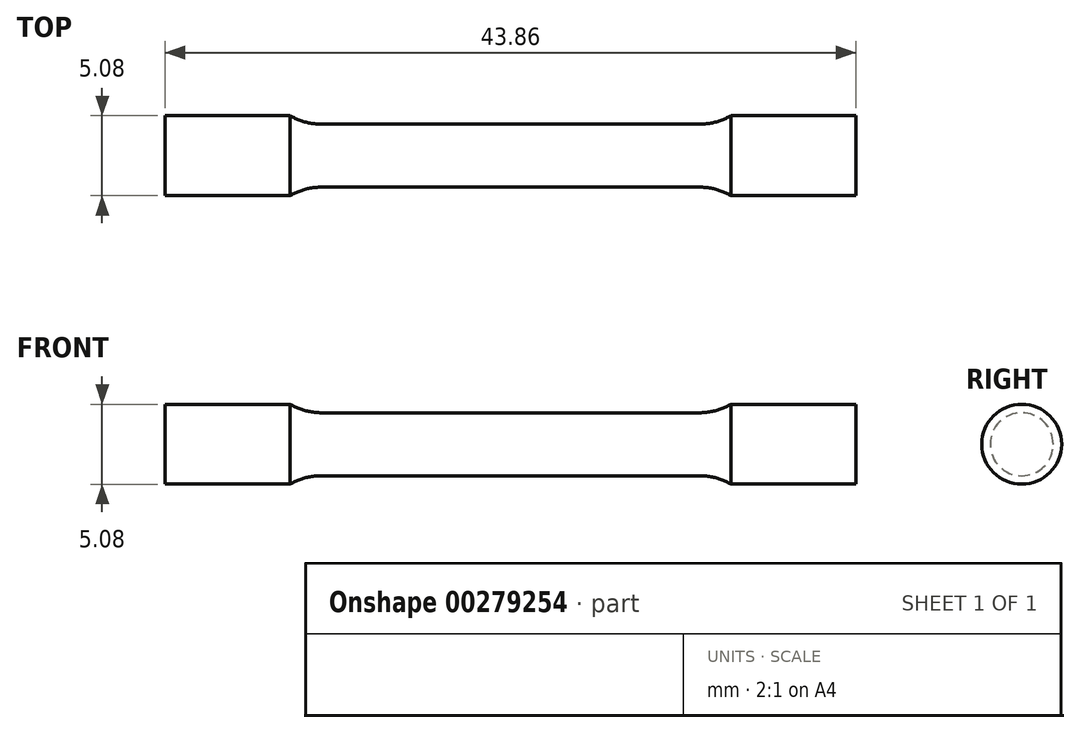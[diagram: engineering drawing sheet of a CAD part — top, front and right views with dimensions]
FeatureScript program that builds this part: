
annotation { "Feature Type Name" : "Feature", "Feature Type Description" : "" }
export const myFeature = defineFeature(function(context is Context, id is Id, definition is map)
    precondition{}
    {
        {
            var Q0;
            Q0=qCreatedBy(makeId("Front.planeOp"),FACE);
            var sketch = newSketch(context, id + "F0", { "sketchPlane" : qUnion([Q0])});
            skLineSegment(sketch, "E0", {"start": v(0, 2) * mm, "end": v(12, 2) * mm});
            skArc(sketch, "E1", {"start": v(12, 2) * mm, "mid": v(13.04, 2.14) * mm, "end": v(14, 2.54) * mm});
            skLineSegment(sketch, "E2", {"start": v(14, 2.54) * mm, "end": v(21.93, 2.54) * mm});
            skLineSegment(sketch, "E3", {"start": v(21.93, 2.54) * mm, "end": v(21.93, 0) * mm});
            skLineSegment(sketch, "E4.MirrorCS", {"start": v(-14, 2.54) * mm, "end": v(-21.93, 2.54) * mm});
            skLineSegment(sketch, "E5.MirrorCS", {"start": v(-21.93, 2.54) * mm, "end": v(-21.93, 0) * mm});
            skLineSegment(sketch, "E6.MirrorCS", {"start": v(0, 2) * mm, "end": v(-12, 2) * mm});
            skArc(sketch, "E7.MirrorCS", {"start": v(-12, 2) * mm, "mid": v(-13.04, 2.14) * mm, "end": v(-14, 2.54) * mm});
            skLineSegment(sketch, "E8", {"start": v(-21.93, 0) * mm, "end": v(21.93, 0) * mm});
            skSolve(sketch);
        }
        {
            var Q0;
            Q0=makeQuery(id+"F0.imprint","IMPRINT",FACE,{"disambiguationData":[TD([[makeQuery(id+"F0.imprint","IMPRINT",EDGE,{"derivedFrom":sQuery(id+"F0.wireOp",EDGE,"E0")}),-1.0]])]});
            var Q1;
            Q1=sQuery(id+"F0.wireOp",EDGE,"E8");
            revolve(context, id + "F1", {"entities" : qUnion([Q0]), "axis" : qUnion([Q1]), "revolveType" : RevolveType.FULL});
        }
    });
